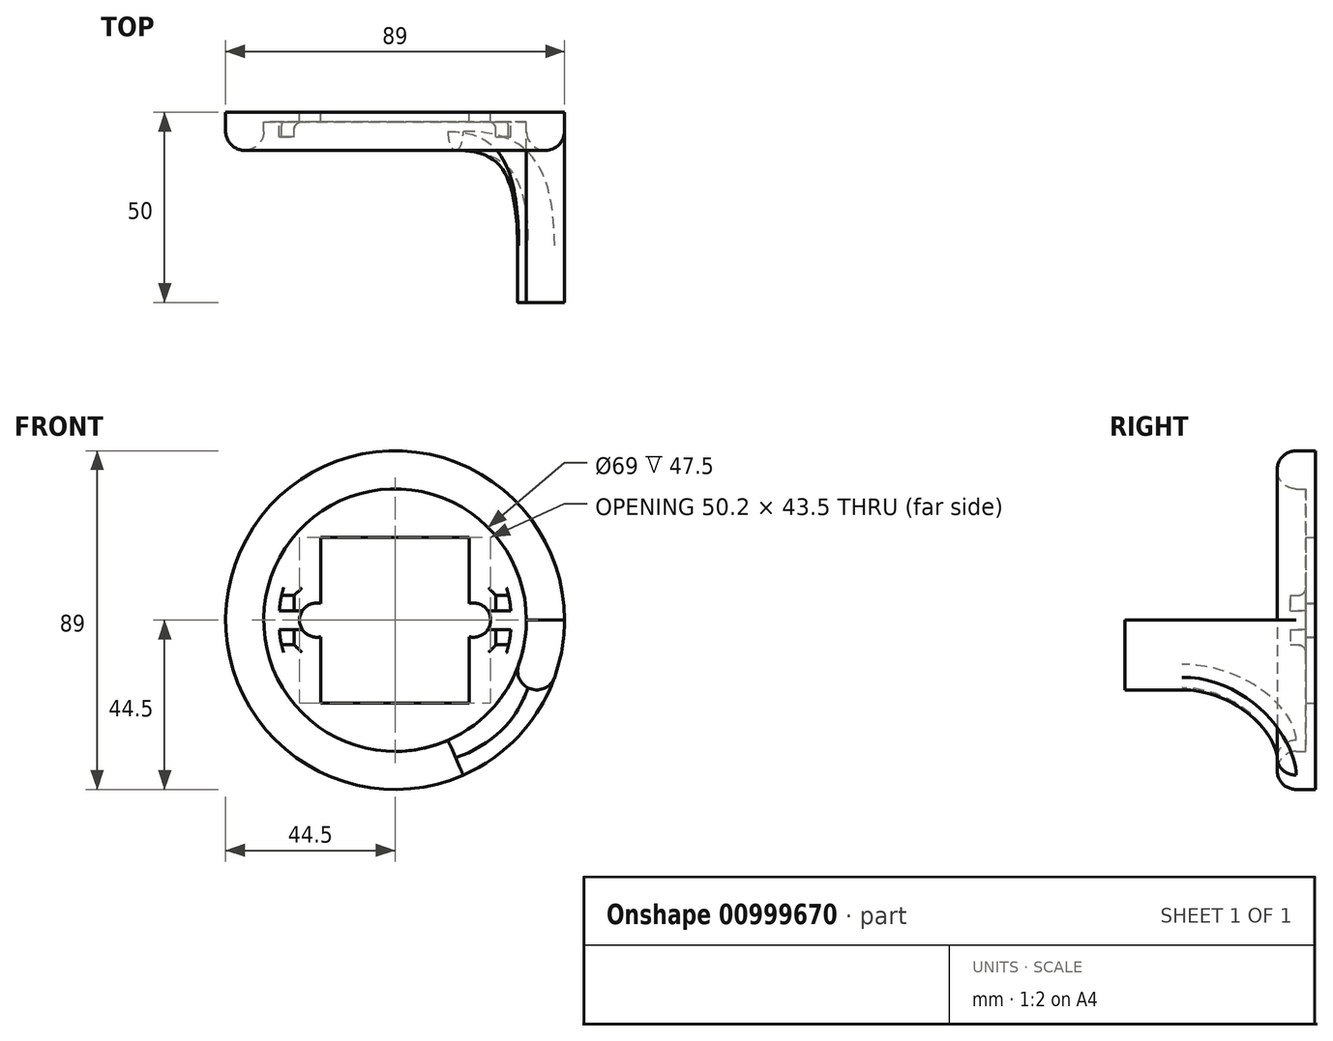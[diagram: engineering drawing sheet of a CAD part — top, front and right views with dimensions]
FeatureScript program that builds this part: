
annotation { "Feature Type Name" : "Feature", "Feature Type Description" : "" }
export const myFeature = defineFeature(function(context is Context, id is Id, definition is map)
    precondition{}
    {
        {
            var Q0;
            Q0=qCreatedBy(makeId("Front.planeOp"),FACE);
            var sketch = newSketch(context, id + "F0", { "sketchPlane" : qUnion([Q0])});
            skCircle(sketch, "E0", {"center": v(0, 0) * mm, "radius": 34.5 * mm});
            skCircle(sketch, "E1", {"center": v(0, 0) * mm, "radius": 44.5 * mm});
            skLineSegment(sketch, "E2", {"start": v(30.74, -15.66) * mm, "end": v(39.65, -20.2) * mm});
            skLineSegment(sketch, "E3", {"start": v(34.5, 0) * mm, "end": v(44.5, 0) * mm});
            skCircle(sketch, "E4", {"center": v(-20.6, 0) * mm, "radius": 4.5 * mm});
            skCircle(sketch, "E5.MirrorC", {"center": v(20.6, 0) * mm, "radius": 4.5 * mm});
            skCircle(sketch, "E6", {"center": v(0, 0) * mm, "radius": 16 * mm});
            skArc(sketch, "E7", {"start": v(4.5, 17.5) * mm, "mid": v(6, 19) * mm, "end": v(4.5, 20.5) * mm});
            skLineSegment(sketch, "E8", {"start": v(4.5, 20.5) * mm, "end": v(0, 20.5) * mm});
            skLineSegment(sketch, "E9", {"start": v(4.5, 17.5) * mm, "end": v(0, 17.5) * mm});
            skLineSegment(sketch, "E10.MirrorCS", {"start": v(-4.5, 17.5) * mm, "end": v(0, 17.5) * mm});
            skArc(sketch, "E11.MirrorCS", {"start": v(-4.5, 17.5) * mm, "mid": v(-6, 19) * mm, "end": v(-4.5, 20.5) * mm});
            skLineSegment(sketch, "E12.MirrorCS", {"start": v(-4.5, 20.5) * mm, "end": v(0, 20.5) * mm});
            skLineSegment(sketch, "E13.MirrorCS", {"start": v(-4.5, -17.5) * mm, "end": v(0, -17.5) * mm});
            skArc(sketch, "E14.MirrorCS", {"start": v(4.5, -17.5) * mm, "mid": v(6, -19) * mm, "end": v(4.5, -20.5) * mm});
            skArc(sketch, "E15.MirrorCS", {"start": v(-4.5, -17.5) * mm, "mid": v(-6, -19) * mm, "end": v(-4.5, -20.5) * mm});
            skLineSegment(sketch, "E16.MirrorCS", {"start": v(4.5, -17.5) * mm, "end": v(0, -17.5) * mm});
            skLineSegment(sketch, "E17.MirrorCS", {"start": v(-4.5, -20.5) * mm, "end": v(0, -20.5) * mm});
            skLineSegment(sketch, "E18.MirrorCS", {"start": v(4.5, -20.5) * mm, "end": v(0, -20.5) * mm});
            skLineSegment(sketch, "E19.trimOffspring", {"start": v(19.5, 21.75) * mm, "end": v(-19.5, 21.75) * mm});
            skLineSegment(sketch, "E20.trimOffspring", {"start": v(-19.5, 21.75) * mm, "end": v(-19.5, -21.75) * mm});
            skLineSegment(sketch, "E21.trimOffspring", {"start": v(19.5, 21.75) * mm, "end": v(19.5, -21.75) * mm});
            skLineSegment(sketch, "E22.trimOffspring", {"start": v(19.5, -21.75) * mm, "end": v(-19.5, -21.75) * mm});
            skPoint(sketch, "E23.trimOffspring.end.orphan", {"position": v(19.5, -59.57) * mm});
            skPoint(sketch, "E24.trimOffspring.end.orphan", {"position": v(-19.5, -59.57) * mm});
            skPoint(sketch, "E25.start.orphan", {"position": v(-19.5, 57.03) * mm});
            skPoint(sketch, "E26.MirrorCS.start.orphan", {"position": v(19.5, 57.03) * mm});
            skLineSegment(sketch, "E27", {"start": v(-30.4, 2.5) * mm, "end": v(-26.5, 2.5) * mm});
            skLineSegment(sketch, "E28", {"start": v(-26.5, 2.5) * mm, "end": v(-26.5, 6.5) * mm});
            skLineSegment(sketch, "E29", {"start": v(-26.5, 6.5) * mm, "end": v(-29.8, 6.5) * mm});
            skLineSegment(sketch, "E30.MirrorCS", {"start": v(-30.4, -2.5) * mm, "end": v(-26.5, -2.5) * mm});
            skLineSegment(sketch, "E31.MirrorCS", {"start": v(-26.5, -2.5) * mm, "end": v(-26.5, -6.5) * mm});
            skLineSegment(sketch, "E32.MirrorCS", {"start": v(-26.5, -6.5) * mm, "end": v(-29.8, -6.5) * mm});
            skLineSegment(sketch, "E33.MirrorCS", {"start": v(26.5, -6.5) * mm, "end": v(29.8, -6.5) * mm});
            skLineSegment(sketch, "E34.MirrorCS", {"start": v(26.5, -2.5) * mm, "end": v(26.5, -6.5) * mm});
            skLineSegment(sketch, "E35.MirrorCS", {"start": v(30.4, -2.5) * mm, "end": v(26.5, -2.5) * mm});
            skLineSegment(sketch, "E36.MirrorCS", {"start": v(30.4, 2.5) * mm, "end": v(26.5, 2.5) * mm});
            skLineSegment(sketch, "E37.MirrorCS", {"start": v(26.5, 2.5) * mm, "end": v(26.5, 6.5) * mm});
            skLineSegment(sketch, "E38.MirrorCS", {"start": v(26.5, 6.5) * mm, "end": v(29.8, 6.5) * mm});
            skCircle(sketch, "E39", {"center": v(0, 0) * mm, "radius": 30.5 * mm});
            skPoint(sketch, "E40.orphan", {"position": v(-34.4, 2.5) * mm});
            skPoint(sketch, "E41.orphan", {"position": v(-33.88, 6.5) * mm});
            skPoint(sketch, "E42.orphan", {"position": v(-34.4, -2.5) * mm});
            skPoint(sketch, "E43.orphan", {"position": v(-33.88, -6.5) * mm});
            skPoint(sketch, "E44.orphan", {"position": v(34.4, 2.5) * mm});
            skPoint(sketch, "E45.orphan", {"position": v(33.88, 6.5) * mm});
            skPoint(sketch, "E46.orphan", {"position": v(33.88, -6.5) * mm});
            skPoint(sketch, "E47.orphan", {"position": v(34.4, -2.5) * mm});
            skLineSegment(sketch, "E48.MirrorCS", {"start": v(-34.5, 0) * mm, "end": v(-44.5, 0) * mm});
            skLineSegment(sketch, "E49.MirrorCS", {"start": v(-30.74, -15.66) * mm, "end": v(-39.65, -20.2) * mm});
            skSolve(sketch);
        }
        {
            var Q0;
            Q0=makeQuery(id+"F0.imprint","IMPRINT",FACE,{"disambiguationData":[TD([[makeQuery(id+"F0.imprint","IMPRINT",EDGE,{"derivedFrom":sQuery(id+"F0.wireOp",EDGE,"E0")}),-1.0]])]});
            extrude(context, id + "F1", {"entities" : qUnion([Q0]), "depth" : 10 * mm, "offsetDistance" : 25 * mm});
        }
        {
            var Q0;
            {var subQ0=sQuery(id+"F0.wireOp",EDGE,"E2");Q0=makeQuery(id+"F0.imprint","IMPRINT",FACE,{"disambiguationData":[TD([[makeQuery(id+"F0.imprint","IMPRINT",EDGE,{"derivedFrom":subQ0}),1.0]])]});}
            extrude(context, id + "F2", {"entities" : qUnion([Q0]), "operationType" : NewBodyOperationType.ADD, "depth" : 50 * mm, "offsetDistance" : 25 * mm});
        }
        {
            var Q0;
            {var subQ0=sQuery(id+"F0.wireOp",EDGE,"E0");var subQ1=makeQuery(id+"F0.imprint","INTERSECT",VERTEX,{"derivedFrom":[subQ0,sQuery(id+"F0.wireOp",EDGE,"E2")]});Q0=makeQuery(id+"F0.imprint","IMPRINT",FACE,{"disambiguationData":[TD([[makeQuery(id+"F0.imprint","IMPRINT",EDGE,{"disambiguationData":[TD([[subQ1,1.0]])],"derivedFrom":subQ0}),1.0]])]});}
            var Q1;
            {var subQ0=sQuery(id+"F0.wireOp",EDGE,"E27");Q1=makeQuery(id+"F0.imprint","IMPRINT",FACE,{"disambiguationData":[TD([[makeQuery(id+"F0.imprint","IMPRINT",EDGE,{"derivedFrom":subQ0}),1.0]])]});}
            var Q2;
            {var subQ0=sQuery(id+"F0.wireOp",EDGE,"E30.MirrorCS");Q2=makeQuery(id+"F0.imprint","IMPRINT",FACE,{"disambiguationData":[TD([[makeQuery(id+"F0.imprint","IMPRINT",EDGE,{"derivedFrom":subQ0}),-1.0]])]});}
            var Q3;
            {var subQ0=sQuery(id+"F0.wireOp",EDGE,"E36.MirrorCS");Q3=makeQuery(id+"F0.imprint","IMPRINT",FACE,{"disambiguationData":[TD([[makeQuery(id+"F0.imprint","IMPRINT",EDGE,{"derivedFrom":subQ0}),-1.0]])]});}
            var Q4;
            {var subQ0=sQuery(id+"F0.wireOp",EDGE,"E33.MirrorCS");Q4=makeQuery(id+"F0.imprint","IMPRINT",FACE,{"disambiguationData":[TD([[makeQuery(id+"F0.imprint","IMPRINT",EDGE,{"derivedFrom":subQ0}),1.0]])]});}
            var Q5;
            {var subQ15=sQuery(id+"F0.wireOp",EDGE,"E27");Q5=makeQuery(id+"F0.imprint","IMPRINT",FACE,{"disambiguationData":[TD([[makeQuery(id+"F0.imprint","IMPRINT",EDGE,{"derivedFrom":subQ15}),-1.0]])]});}
            extrude(context, id + "F3", {"entities" : qUnion([Q0, Q1, Q2, Q3, Q4, Q5]), "operationType" : NewBodyOperationType.ADD, "depth" : 2.5 * mm, "offsetDistance" : 25 * mm});
        }
        {
            var Q0;
            {var subQ0=sQuery(id+"F0.wireOp",EDGE,"E27");Q0=makeQuery(id+"F0.imprint","IMPRINT",FACE,{"disambiguationData":[TD([[makeQuery(id+"F0.imprint","IMPRINT",EDGE,{"derivedFrom":subQ0}),1.0]])]});}
            var Q1;
            {var subQ0=sQuery(id+"F0.wireOp",EDGE,"E30.MirrorCS");Q1=makeQuery(id+"F0.imprint","IMPRINT",FACE,{"disambiguationData":[TD([[makeQuery(id+"F0.imprint","IMPRINT",EDGE,{"derivedFrom":subQ0}),-1.0]])]});}
            var Q2;
            {var subQ0=sQuery(id+"F0.wireOp",EDGE,"E36.MirrorCS");Q2=makeQuery(id+"F0.imprint","IMPRINT",FACE,{"disambiguationData":[TD([[makeQuery(id+"F0.imprint","IMPRINT",EDGE,{"derivedFrom":subQ0}),-1.0]])]});}
            var Q3;
            {var subQ0=sQuery(id+"F0.wireOp",EDGE,"E33.MirrorCS");Q3=makeQuery(id+"F0.imprint","IMPRINT",FACE,{"disambiguationData":[TD([[makeQuery(id+"F0.imprint","IMPRINT",EDGE,{"derivedFrom":subQ0}),1.0]])]});}
            extrude(context, id + "F4", {"entities" : qUnion([Q0, Q1, Q2, Q3]), "operationType" : NewBodyOperationType.ADD, "depth" : 6.5 * mm, "offsetDistance" : 25 * mm});
        }
        {
            var Q0;
            Q0=makeQuery(id+"F4.boolean.opBoolean","INTERSECT",EDGE,{"derivedFrom":[makeQuery(id+"F3.opExtrude","CAP_FACE",FACE,{"disambiguationData":[OSD([sQuery(id+"F0.wireOp",EDGE,"E0"),sQuery(id+"F0.wireOp",EDGE,"E4"),sQuery(id+"F0.wireOp",EDGE,"E5.MirrorC"),sQuery(id+"F0.wireOp",EDGE,"E19.trimOffspring"),sQuery(id+"F0.wireOp",EDGE,"E20.trimOffspring"),sQuery(id+"F0.wireOp",EDGE,"E21.trimOffspring"),sQuery(id+"F0.wireOp",EDGE,"E22.trimOffspring")])],"isStart":false}),makeQuery(id+"F4.opExtrude","SWEPT_FACE",FACE,{"disambiguationData":[OSD([sQuery(id+"F0.wireOp",EDGE,"E28")])]})]});
            var Q1;
            Q1=makeQuery(id+"F4.boolean.opBoolean","INTERSECT",EDGE,{"derivedFrom":[makeQuery(id+"F3.opExtrude","CAP_FACE",FACE,{"disambiguationData":[OSD([sQuery(id+"F0.wireOp",EDGE,"E0"),sQuery(id+"F0.wireOp",EDGE,"E4"),sQuery(id+"F0.wireOp",EDGE,"E5.MirrorC"),sQuery(id+"F0.wireOp",EDGE,"E19.trimOffspring"),sQuery(id+"F0.wireOp",EDGE,"E20.trimOffspring"),sQuery(id+"F0.wireOp",EDGE,"E21.trimOffspring"),sQuery(id+"F0.wireOp",EDGE,"E22.trimOffspring")])],"isStart":false}),makeQuery(id+"F4.opExtrude","SWEPT_FACE",FACE,{"disambiguationData":[OSD([sQuery(id+"F0.wireOp",EDGE,"E29")])]})]});
            var Q2;
            Q2=makeQuery(id+"F4.boolean.opBoolean","INTERSECT",EDGE,{"derivedFrom":[makeQuery(id+"F3.opExtrude","CAP_FACE",FACE,{"disambiguationData":[OSD([sQuery(id+"F0.wireOp",EDGE,"E0"),sQuery(id+"F0.wireOp",EDGE,"E4"),sQuery(id+"F0.wireOp",EDGE,"E5.MirrorC"),sQuery(id+"F0.wireOp",EDGE,"E19.trimOffspring"),sQuery(id+"F0.wireOp",EDGE,"E20.trimOffspring"),sQuery(id+"F0.wireOp",EDGE,"E21.trimOffspring"),sQuery(id+"F0.wireOp",EDGE,"E22.trimOffspring")])],"isStart":false}),makeQuery(id+"F4.opExtrude","SWEPT_FACE",FACE,{"disambiguationData":[OSD([sQuery(id+"F0.wireOp",EDGE,"E31.MirrorCS")])]})]});
            var Q3;
            Q3=makeQuery(id+"F4.boolean.opBoolean","INTERSECT",EDGE,{"derivedFrom":[makeQuery(id+"F3.opExtrude","CAP_FACE",FACE,{"disambiguationData":[OSD([sQuery(id+"F0.wireOp",EDGE,"E0"),sQuery(id+"F0.wireOp",EDGE,"E4"),sQuery(id+"F0.wireOp",EDGE,"E5.MirrorC"),sQuery(id+"F0.wireOp",EDGE,"E19.trimOffspring"),sQuery(id+"F0.wireOp",EDGE,"E20.trimOffspring"),sQuery(id+"F0.wireOp",EDGE,"E21.trimOffspring"),sQuery(id+"F0.wireOp",EDGE,"E22.trimOffspring")])],"isStart":false}),makeQuery(id+"F4.opExtrude","SWEPT_FACE",FACE,{"disambiguationData":[OSD([sQuery(id+"F0.wireOp",EDGE,"E32.MirrorCS")])]})]});
            var Q4;
            Q4=makeQuery(id+"F4.boolean.opBoolean","INTERSECT",EDGE,{"derivedFrom":[makeQuery(id+"F3.opExtrude","CAP_FACE",FACE,{"disambiguationData":[OSD([sQuery(id+"F0.wireOp",EDGE,"E0"),sQuery(id+"F0.wireOp",EDGE,"E4"),sQuery(id+"F0.wireOp",EDGE,"E5.MirrorC"),sQuery(id+"F0.wireOp",EDGE,"E19.trimOffspring"),sQuery(id+"F0.wireOp",EDGE,"E20.trimOffspring"),sQuery(id+"F0.wireOp",EDGE,"E21.trimOffspring"),sQuery(id+"F0.wireOp",EDGE,"E22.trimOffspring")])],"isStart":false}),makeQuery(id+"F4.opExtrude","SWEPT_FACE",FACE,{"disambiguationData":[OSD([sQuery(id+"F0.wireOp",EDGE,"E33.MirrorCS")])]})]});
            var Q5;
            Q5=makeQuery(id+"F4.boolean.opBoolean","INTERSECT",EDGE,{"derivedFrom":[makeQuery(id+"F3.opExtrude","CAP_FACE",FACE,{"disambiguationData":[OSD([sQuery(id+"F0.wireOp",EDGE,"E0"),sQuery(id+"F0.wireOp",EDGE,"E4"),sQuery(id+"F0.wireOp",EDGE,"E5.MirrorC"),sQuery(id+"F0.wireOp",EDGE,"E19.trimOffspring"),sQuery(id+"F0.wireOp",EDGE,"E20.trimOffspring"),sQuery(id+"F0.wireOp",EDGE,"E21.trimOffspring"),sQuery(id+"F0.wireOp",EDGE,"E22.trimOffspring")])],"isStart":false}),makeQuery(id+"F4.opExtrude","SWEPT_FACE",FACE,{"disambiguationData":[OSD([sQuery(id+"F0.wireOp",EDGE,"E34.MirrorCS")])]})]});
            var Q6;
            Q6=makeQuery(id+"F4.boolean.opBoolean","INTERSECT",EDGE,{"derivedFrom":[makeQuery(id+"F3.opExtrude","CAP_FACE",FACE,{"disambiguationData":[OSD([sQuery(id+"F0.wireOp",EDGE,"E0"),sQuery(id+"F0.wireOp",EDGE,"E4"),sQuery(id+"F0.wireOp",EDGE,"E5.MirrorC"),sQuery(id+"F0.wireOp",EDGE,"E19.trimOffspring"),sQuery(id+"F0.wireOp",EDGE,"E20.trimOffspring"),sQuery(id+"F0.wireOp",EDGE,"E21.trimOffspring"),sQuery(id+"F0.wireOp",EDGE,"E22.trimOffspring")])],"isStart":false}),makeQuery(id+"F4.opExtrude","SWEPT_FACE",FACE,{"disambiguationData":[OSD([sQuery(id+"F0.wireOp",EDGE,"E37.MirrorCS")])]})]});
            var Q7;
            Q7=makeQuery(id+"F4.boolean.opBoolean","INTERSECT",EDGE,{"derivedFrom":[makeQuery(id+"F3.opExtrude","CAP_FACE",FACE,{"disambiguationData":[OSD([sQuery(id+"F0.wireOp",EDGE,"E0"),sQuery(id+"F0.wireOp",EDGE,"E4"),sQuery(id+"F0.wireOp",EDGE,"E5.MirrorC"),sQuery(id+"F0.wireOp",EDGE,"E19.trimOffspring"),sQuery(id+"F0.wireOp",EDGE,"E20.trimOffspring"),sQuery(id+"F0.wireOp",EDGE,"E21.trimOffspring"),sQuery(id+"F0.wireOp",EDGE,"E22.trimOffspring")])],"isStart":false}),makeQuery(id+"F4.opExtrude","SWEPT_FACE",FACE,{"disambiguationData":[OSD([sQuery(id+"F0.wireOp",EDGE,"E38.MirrorCS")])]})]});
            fillet(context, id + "F5", {"entities" : qUnion([Q0, Q1, Q2, Q3, Q4, Q5, Q6, Q7]), "radius" : 2 * mm, "tangentPropagation" : true, "allowEdgeOverflow" : false});
        }
        {
            var Q0;
            Q0=makeQuery(id+"F2.boolean.opBoolean","INTERSECT",EDGE,{"derivedFrom":[makeQuery(id+"F1.opExtrude","CAP_FACE",FACE,{"disambiguationData":[OSD([sQuery(id+"F0.wireOp",EDGE,"E0"),sQuery(id+"F0.wireOp",EDGE,"E1")])],"isStart":false}),makeQuery(id+"F2.opExtrude","SWEPT_FACE",FACE,{"disambiguationData":[OSD([sQuery(id+"F0.wireOp",EDGE,"E2")])]})]});
            fillet(context, id + "F6", {"entities" : qUnion([Q0]), "radius" : 25 * mm, "tangentPropagation" : true, "allowEdgeOverflow" : false});
        }
        {
            var Q0;
            Q0=makeQuery(id+"F1.opExtrude","CAP_EDGE",EDGE,{"disambiguationData":[OSD([sQuery(id+"F0.wireOp",EDGE,"E1")])],"isStart":false});
            var Q1;
            Q1=makeQuery(id+"F1.opExtrude","CAP_EDGE",EDGE,{"disambiguationData":[OSD([sQuery(id+"F0.wireOp",EDGE,"E0")])],"isStart":false});
            fillet(context, id + "F7", {"entities" : qUnion([Q0, Q1]), "radius" : 5 * mm, "tangentPropagation" : true, "allowEdgeOverflow" : false});
        }
    });
